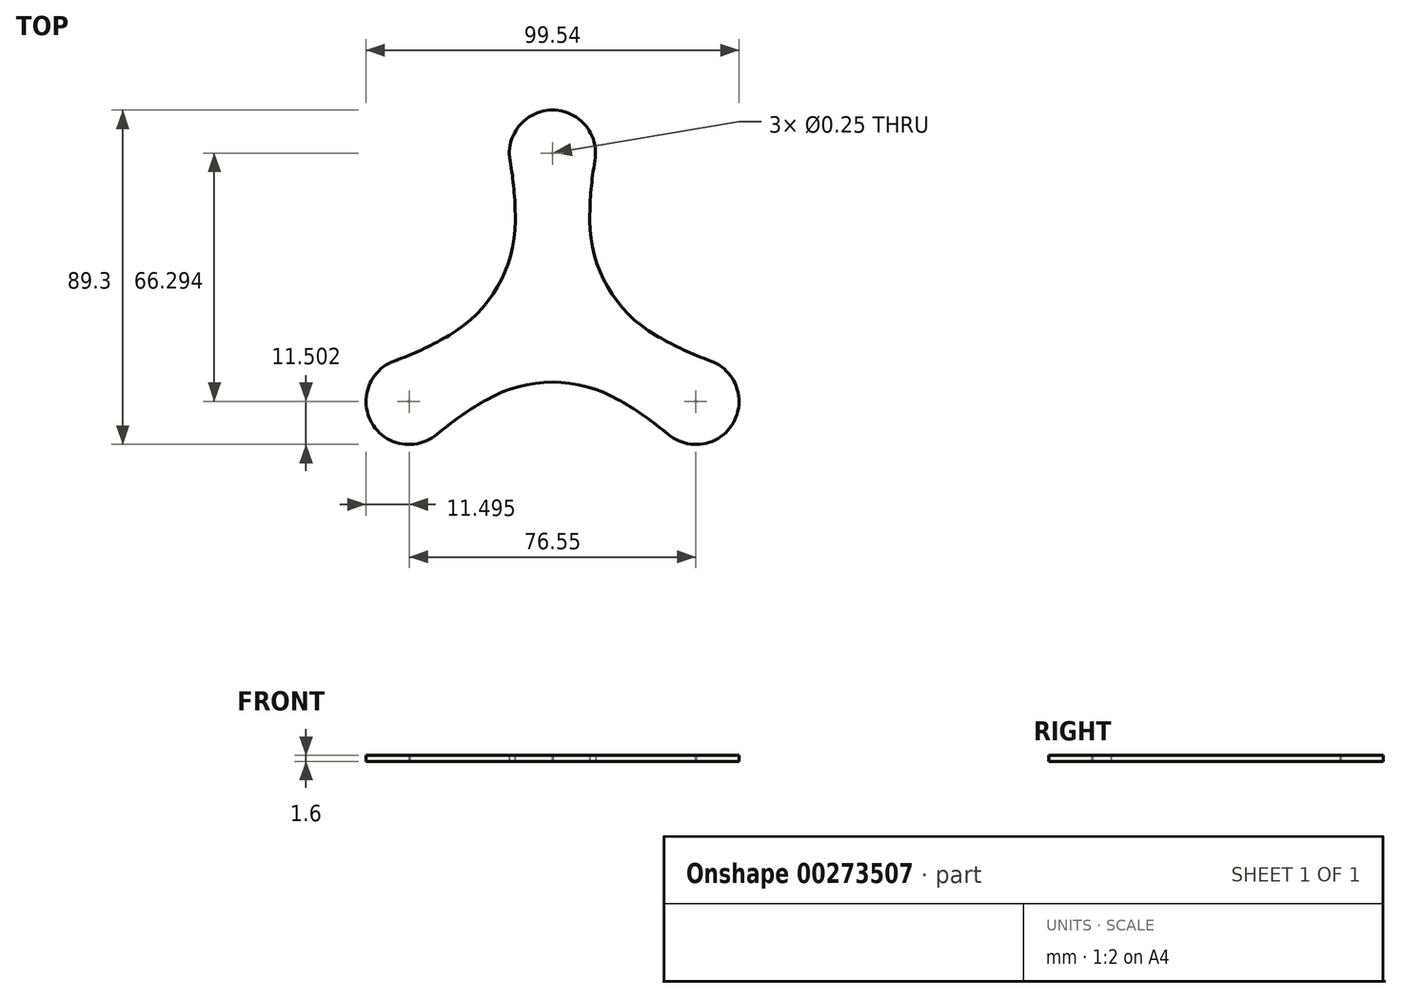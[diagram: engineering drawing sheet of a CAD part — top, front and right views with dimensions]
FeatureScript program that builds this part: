
annotation { "Feature Type Name" : "Feature", "Feature Type Description" : "" }
export const myFeature = defineFeature(function(context is Context, id is Id, definition is map)
    precondition{}
    {
        {
            assignVariable(context, id + "F0", {"variableType" : VariableType.NUMBER, "name" : "scale", "numberValue" : 0.87});
        }
        {
            var Q0;
            Q0=qCreatedBy(makeId("Top.planeOp"),FACE);
            var sketch = newSketch(context, id + "F1", { "sketchPlane" : qUnion([Q0])});
            skCircle(sketch, "E0", {"center": v(0, 44.2) * mm, "radius": 9.6 * mm, "construction": true});
            skCircle(sketch, "E1", {"center": v(0, 44.2) * mm, "radius": 11.5 * mm, "construction": true});
            skCircle(sketch, "E2", {"center": v(0, 53.8) * mm, "radius": 1.5 * mm, "construction": true});
            skLineSegment(sketch, "E3", {"start": v(0, 44.2) * mm, "end": v(0, 55.7) * mm, "construction": true});
            skLineSegment(sketch, "E4.1.0", {"start": v(0, 44.2) * mm, "end": v(-9.96, 38.45) * mm, "construction": true});
            skCircle(sketch, "E4.1.1", {"center": v(-8.31, 39.4) * mm, "radius": 1.5 * mm, "construction": true});
            skLineSegment(sketch, "E4.2.0", {"start": v(0, 44.2) * mm, "end": v(9.96, 38.45) * mm, "construction": true});
            skCircle(sketch, "E4.2.1", {"center": v(8.31, 39.4) * mm, "radius": 1.5 * mm, "construction": true});
            skArc(sketch, "E5", {"start": v(9.96, 38.45) * mm, "mid": v(0, 55.7) * mm, "end": v(-9.96, 38.45) * mm});
            skLineSegment(sketch, "E6", {"start": v(-9.96, 38.45) * mm, "end": v(-9.96, 26.1) * mm});
            skLineSegment(sketch, "E7", {"start": v(9.96, 38.45) * mm, "end": v(9.96, 26.1) * mm});
            skLineSegment(sketch, "E8.1.0", {"start": v(-38.27, -22.1) * mm, "end": v(-48.23, -27.85) * mm, "construction": true});
            skPoint(sketch, "E8.1.1", {"position": v(-38.27, -22.1) * mm});
            skLineSegment(sketch, "E8.1.2", {"start": v(-38.27, -22.1) * mm, "end": v(-38.27, -10.6) * mm, "construction": true});
            skCircle(sketch, "E8.1.3", {"center": v(-38.27, -22.1) * mm, "radius": 11.5 * mm, "construction": true});
            skCircle(sketch, "E8.1.4", {"center": v(-38.27, -22.1) * mm, "radius": 9.6 * mm, "construction": true});
            skLineSegment(sketch, "E8.1.5", {"start": v(-28.32, -27.85) * mm, "end": v(-17.62, -21.67) * mm});
            skLineSegment(sketch, "E8.1.6", {"start": v(-38.27, -22.1) * mm, "end": v(-28.32, -27.85) * mm, "construction": true});
            skLineSegment(sketch, "E8.1.7", {"start": v(-38.27, -10.6) * mm, "end": v(-27.58, -4.42) * mm});
            skCircle(sketch, "E8.1.8", {"center": v(-29.96, -26.9) * mm, "radius": 1.5 * mm, "construction": true});
            skCircle(sketch, "E8.1.9", {"center": v(-38.27, -12.5) * mm, "radius": 1.5 * mm, "construction": true});
            skPoint(sketch, "E8.1.10", {"position": v(-38.27, -22.1) * mm});
            skCircle(sketch, "E8.1.11", {"center": v(-46.59, -26.9) * mm, "radius": 1.5 * mm, "construction": true});
            skArc(sketch, "E8.1.12", {"start": v(-38.27, -10.6) * mm, "mid": v(-48.23, -27.85) * mm, "end": v(-28.32, -27.85) * mm});
            skPoint(sketch, "E8.1.13", {"position": v(-38.27, -22.1) * mm});
            skLineSegment(sketch, "E8.2.0", {"start": v(38.27, -22.1) * mm, "end": v(48.23, -27.85) * mm, "construction": true});
            skPoint(sketch, "E8.2.1", {"position": v(38.27, -22.1) * mm});
            skLineSegment(sketch, "E8.2.2", {"start": v(38.27, -22.1) * mm, "end": v(28.32, -27.85) * mm, "construction": true});
            skCircle(sketch, "E8.2.3", {"center": v(38.27, -22.1) * mm, "radius": 11.5 * mm, "construction": true});
            skCircle(sketch, "E8.2.4", {"center": v(38.27, -22.1) * mm, "radius": 9.6 * mm, "construction": true});
            skLineSegment(sketch, "E8.2.5", {"start": v(38.27, -10.6) * mm, "end": v(27.58, -4.43) * mm});
            skLineSegment(sketch, "E8.2.6", {"start": v(38.27, -22.1) * mm, "end": v(38.27, -10.6) * mm, "construction": true});
            skLineSegment(sketch, "E8.2.7", {"start": v(28.32, -27.85) * mm, "end": v(17.62, -21.68) * mm});
            skCircle(sketch, "E8.2.8", {"center": v(38.27, -12.5) * mm, "radius": 1.5 * mm, "construction": true});
            skCircle(sketch, "E8.2.9", {"center": v(29.96, -26.9) * mm, "radius": 1.5 * mm, "construction": true});
            skPoint(sketch, "E8.2.10", {"position": v(38.27, -22.1) * mm});
            skCircle(sketch, "E8.2.11", {"center": v(46.59, -26.9) * mm, "radius": 1.5 * mm, "construction": true});
            skArc(sketch, "E8.2.12", {"start": v(28.32, -27.85) * mm, "mid": v(48.23, -27.85) * mm, "end": v(38.27, -10.6) * mm});
            skPoint(sketch, "E8.2.13", {"position": v(38.27, -22.1) * mm});
            skPoint(sketch, "E8.center", {"position": v(0, 0) * mm});
            skLineSegment(sketch, "E9.bottom", {"start": v(4, -4) * mm, "end": v(-4, -4) * mm, "construction": true});
            skLineSegment(sketch, "E9.top", {"start": v(4, 4) * mm, "end": v(-4, 4) * mm, "construction": true});
            skLineSegment(sketch, "E9.left", {"start": v(4, -4) * mm, "end": v(4, 4) * mm, "construction": true});
            skLineSegment(sketch, "E9.right", {"start": v(-4, -4) * mm, "end": v(-4, 4) * mm, "construction": true});
            skLineSegment(sketch, "E10.bottom", {"start": v(10, -15) * mm, "end": v(-10, -15) * mm, "construction": true});
            skLineSegment(sketch, "E10.top", {"start": v(10, 15) * mm, "end": v(-10, 15) * mm, "construction": true});
            skLineSegment(sketch, "E10.left", {"start": v(10, -15) * mm, "end": v(10, 15) * mm, "construction": true});
            skLineSegment(sketch, "E10.right", {"start": v(-10, -15) * mm, "end": v(-10, 15) * mm, "construction": true});
            skCircle(sketch, "E11", {"center": v(38.27, -22.1) * mm, "radius": 0.13 * mm});
            skCircle(sketch, "E12", {"center": v(0, 44.2) * mm, "radius": 0.13 * mm});
            skCircle(sketch, "E13", {"center": v(-38.27, -22.1) * mm, "radius": 0.13 * mm});
            skArc(sketch, "E14", {"start": v(-27.58, -4.43) * mm, "mid": v(-14.68, 8.48) * mm, "end": v(-9.96, 26.1) * mm});
            skArc(sketch, "E15", {"start": v(9.96, 26.1) * mm, "mid": v(14.68, 8.48) * mm, "end": v(27.58, -4.42) * mm});
            skArc(sketch, "E16", {"start": v(-17.62, -21.68) * mm, "mid": v(0, -16.95) * mm, "end": v(17.62, -21.67) * mm});
            skSolve(sketch);
        }
        {
            var Q0;
            Q0 = qSketchRegion(id + "F1", true);
            extrude(context, id + "F2", {"entities" : qUnion([Q0]), "depth" : 1.6 * mm, "offsetDistance" : 25 * mm});
        }
        {
            var Q0;
            Q0=makeQuery(id+"F2.opExtrude","SWEPT_EDGE",EDGE,{"disambiguationData":[OSD([sQuery(id+"F1.wireOp",EDGE,"E8.1.5"),sQuery(id+"F1.wireOp",EDGE,"E8.1.12")])]});
            var Q1;
            Q1=makeQuery(id+"F2.opExtrude","SWEPT_EDGE",EDGE,{"disambiguationData":[OSD([sQuery(id+"F1.wireOp",EDGE,"E8.1.7"),sQuery(id+"F1.wireOp",EDGE,"E8.1.12")])]});
            var Q2;
            Q2=makeQuery(id+"F2.opExtrude","SWEPT_EDGE",EDGE,{"disambiguationData":[OSD([sQuery(id+"F1.wireOp",EDGE,"E8.2.7"),sQuery(id+"F1.wireOp",EDGE,"E8.2.12")])]});
            var Q3;
            Q3=makeQuery(id+"F2.opExtrude","SWEPT_EDGE",EDGE,{"disambiguationData":[OSD([sQuery(id+"F1.wireOp",EDGE,"E8.2.5"),sQuery(id+"F1.wireOp",EDGE,"E8.2.12")])]});
            var Q4;
            Q4=makeQuery(id+"F2.opExtrude","SWEPT_EDGE",EDGE,{"disambiguationData":[OSD([sQuery(id+"F1.wireOp",EDGE,"E5"),sQuery(id+"F1.wireOp",EDGE,"E7")])]});
            var Q5;
            Q5=makeQuery(id+"F2.opExtrude","SWEPT_EDGE",EDGE,{"disambiguationData":[OSD([sQuery(id+"F1.wireOp",EDGE,"E5"),sQuery(id+"F1.wireOp",EDGE,"E6")])]});
            fillet(context, id + "F3", {"entities" : qUnion([Q0, Q1, Q2, Q3, Q4, Q5]), "tangentPropagation" : true, "radius" : getVariable(context, 'scale') * 100 * mm, "defaultsChanged" : true, "vertexSettings" : [], "allowEdgeOverflow" : false});
        }
    });
